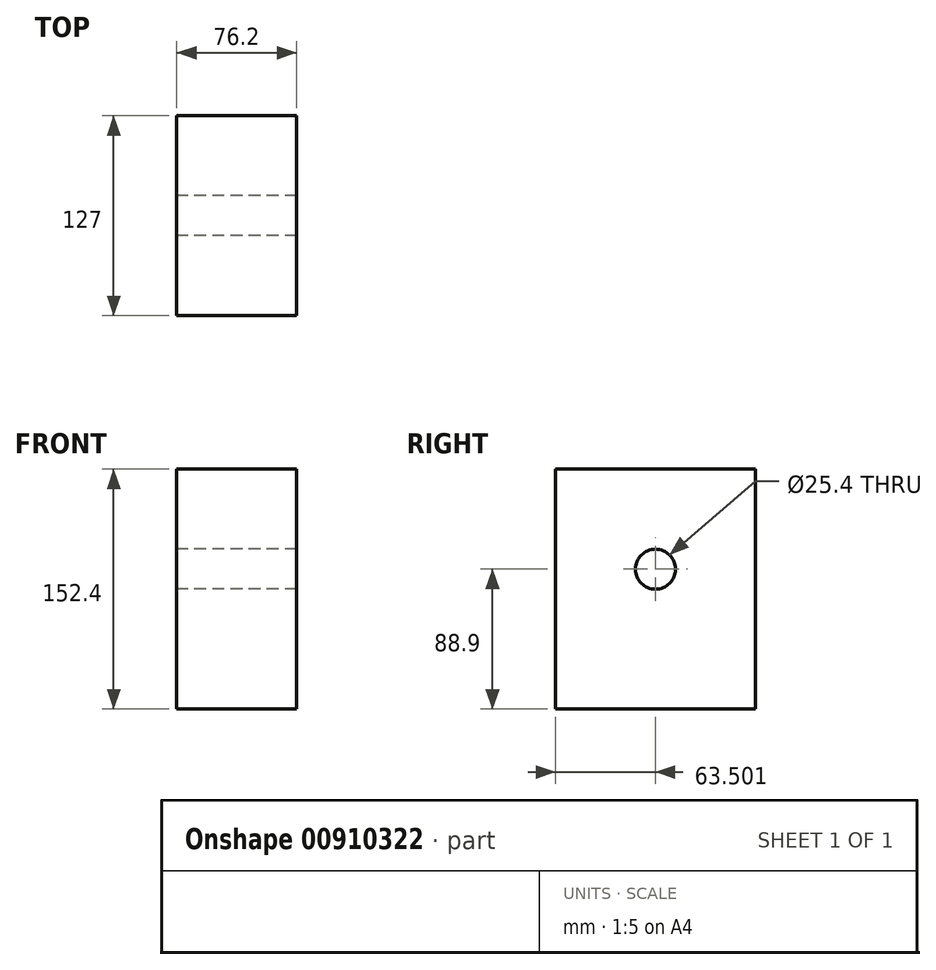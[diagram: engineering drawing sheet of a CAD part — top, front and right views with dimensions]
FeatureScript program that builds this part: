
annotation { "Feature Type Name" : "Feature", "Feature Type Description" : "" }
export const myFeature = defineFeature(function(context is Context, id is Id, definition is map)
    precondition{}
    {
        {
            var Q0;
            Q0=qCreatedBy(makeId("Top.planeOp"),FACE);
            var sketch = newSketch(context, id + "F0", { "sketchPlane" : qUnion([Q0])});
            skLineSegment(sketch, "E0.bottom", {"start": v(102.54, 170.57) * mm, "end": v(26.34, 170.57) * mm});
            skLineSegment(sketch, "E0.top", {"start": v(102.54, 43.57) * mm, "end": v(26.34, 43.57) * mm});
            skLineSegment(sketch, "E0.left", {"start": v(102.54, 170.57) * mm, "end": v(102.54, 43.57) * mm});
            skLineSegment(sketch, "E0.right", {"start": v(26.34, 170.57) * mm, "end": v(26.34, 43.57) * mm});
            skSolve(sketch);
        }
        {
            var Q0;
            Q0=makeQuery(id+"F0.imprint","IMPRINT",FACE,{"disambiguationData":[TD([[makeQuery(id+"F0.imprint","IMPRINT",EDGE,{"derivedFrom":sQuery(id+"F0.wireOp",EDGE,"E0.bottom")}),1.0]])]});
            extrude(context, id + "F1", {"entities" : qUnion([Q0]), "depth" : 152.4 * mm, "offsetDistance" : 25.4 * mm});
        }
        {
            var Q0;
            Q0=makeQuery(id+"F1.opExtrude","SWEPT_FACE",FACE,{"disambiguationData":[OSD([sQuery(id+"F0.wireOp",EDGE,"E0.right")])]});
            var sketch = newSketch(context, id + "F2", { "sketchPlane" : qUnion([Q0])});
            skCircle(sketch, "E1", {"center": v(-107.07, 88.9) * mm, "radius": 12.7 * mm});
            skSolve(sketch);
        }
        {
            var Q0;
            Q0=makeQuery(id+"F2.imprint","IMPRINT",FACE,{"disambiguationData":[TD([[makeQuery(id+"F2.imprint","IMPRINT",EDGE,{"derivedFrom":sQuery(id+"F2.wireOp",EDGE,"E1")}),1.0]])]});
            extrude(context, id + "F3", {"entities" : qUnion([Q0]), "operationType" : NewBodyOperationType.REMOVE, "endBound" : BoundingType.THROUGH_ALL, "oppositeDirection" : true, "depth" : 25.4 * mm, "offsetDistance" : 25.4 * mm});
        }
    });
